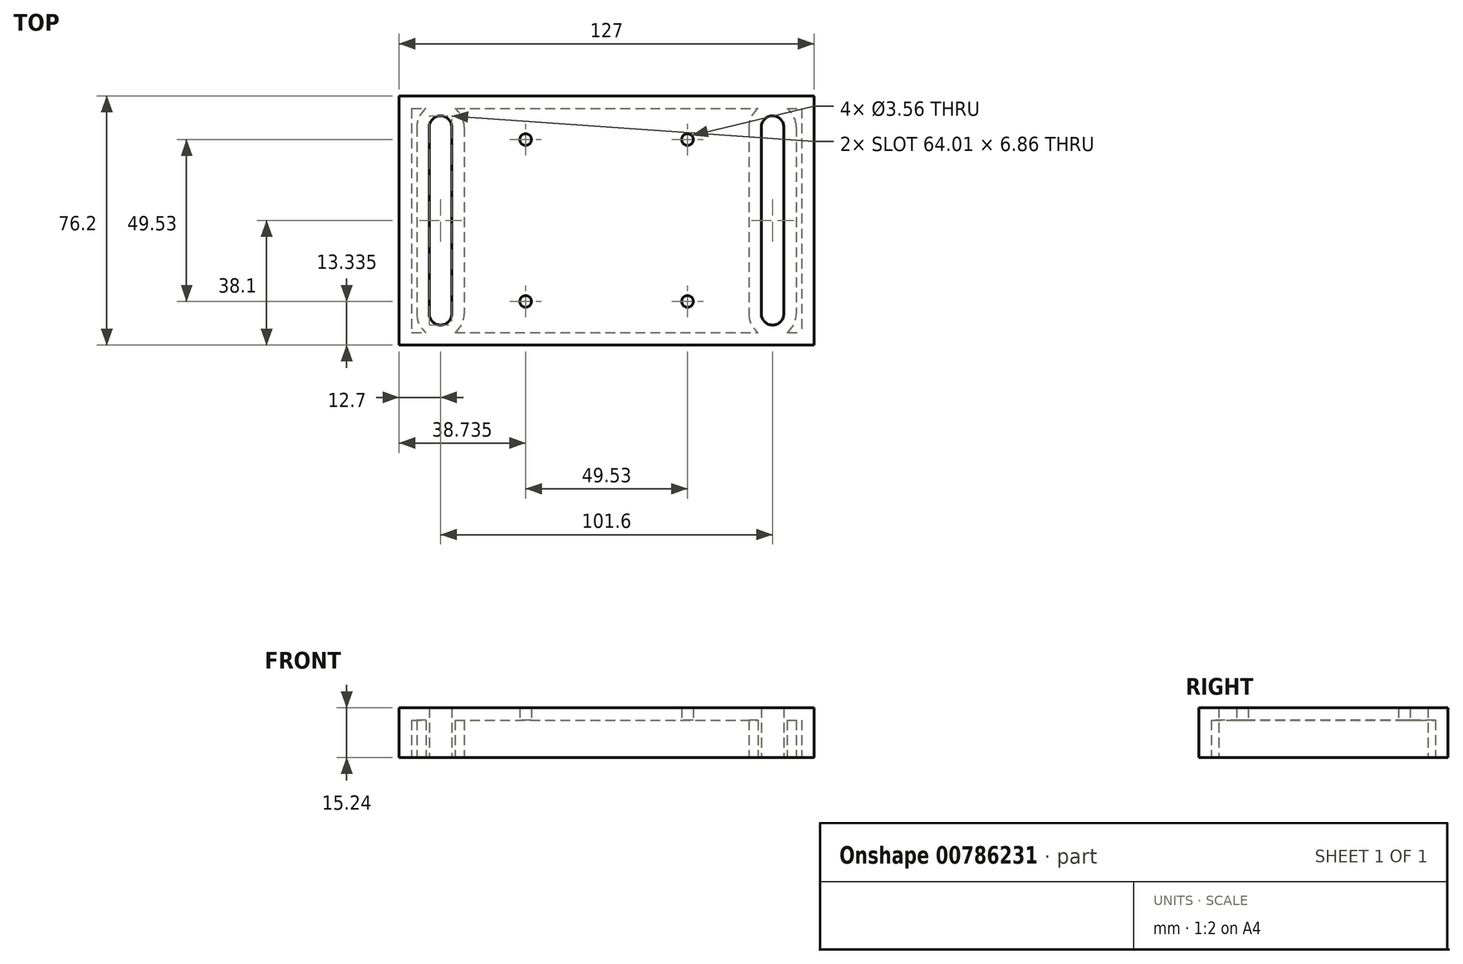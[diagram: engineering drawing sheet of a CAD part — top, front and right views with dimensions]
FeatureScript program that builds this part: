
annotation { "Feature Type Name" : "Feature", "Feature Type Description" : "" }
export const myFeature = defineFeature(function(context is Context, id is Id, definition is map)
    precondition{}
    {
        {
            var Q0;
            Q0=qCreatedBy(makeId("Top.planeOp"),FACE);
            var sketch = newSketch(context, id + "F0", { "sketchPlane" : qUnion([Q0])});
            skLineSegment(sketch, "E0.bottom", {"start": v(-63.5, 38.1) * mm, "end": v(63.5, 38.1) * mm});
            skLineSegment(sketch, "E0.top", {"start": v(-63.5, -38.1) * mm, "end": v(63.5, -38.1) * mm});
            skLineSegment(sketch, "E0.left", {"start": v(-63.5, 38.1) * mm, "end": v(-63.5, -38.1) * mm});
            skLineSegment(sketch, "E0.right", {"start": v(63.5, 38.1) * mm, "end": v(63.5, -38.1) * mm});
            skSolve(sketch);
        }
        {
            var Q0;
            Q0 = qSketchRegion(id + "F0", true);
            extrude(context, id + "F1", {"entities" : qUnion([Q0]), "depth" : 15.24 * mm, "offsetDistance" : 25.4 * mm});
        }
        {
            var Q0;
            Q0=qCreatedBy(makeId("Top.planeOp"),FACE);
            var sketch = newSketch(context, id + "F2", { "sketchPlane" : qUnion([Q0])});
            skLineSegment(sketch, "E1.left", {"start": v(-54.23, 28.58) * mm, "end": v(-54.23, -28.58) * mm});
            skLineSegment(sketch, "E1.right", {"start": v(-47.37, 28.58) * mm, "end": v(-47.37, -28.58) * mm});
            skLineSegment(sketch, "E2.left", {"start": v(47.37, 28.58) * mm, "end": v(47.37, -28.58) * mm});
            skLineSegment(sketch, "E2.right", {"start": v(54.23, 28.58) * mm, "end": v(54.23, -28.58) * mm});
            skArc(sketch, "E3", {"start": v(-47.37, 28.58) * mm, "mid": v(-50.8, 32) * mm, "end": v(-54.23, 28.58) * mm});
            skArc(sketch, "E4", {"start": v(-54.23, -28.58) * mm, "mid": v(-50.8, -32) * mm, "end": v(-47.37, -28.58) * mm});
            skArc(sketch, "E5", {"start": v(47.37, -28.58) * mm, "mid": v(50.8, -32) * mm, "end": v(54.23, -28.58) * mm});
            skArc(sketch, "E6", {"start": v(54.23, 28.58) * mm, "mid": v(50.8, 32) * mm, "end": v(47.37, 28.58) * mm});
            skSolve(sketch);
        }
        {
            var Q0;
            Q0 = qSketchRegion(id + "F2", true);
            extrude(context, id + "F3", {"entities" : qUnion([Q0]), "operationType" : NewBodyOperationType.REMOVE, "endBound" : BoundingType.THROUGH_ALL, "depth" : 25.4 * mm, "offsetDistance" : 25.4 * mm});
        }
        {
            var Q0;
            Q0=makeQuery(id+"F1.opExtrude","CAP_FACE",FACE,{"disambiguationData":[OSD([sQuery(id+"F0.wireOp",EDGE,"E0.bottom"),sQuery(id+"F0.wireOp",EDGE,"E0.top"),sQuery(id+"F0.wireOp",EDGE,"E0.left"),sQuery(id+"F0.wireOp",EDGE,"E0.right")])],"isStart":true});
            shell(context, id + "F4", {"entities" : qUnion([Q0]), "thickness" : 3.8 * mm});
        }
        {
            var Q0;
            Q0=qCreatedBy(makeId("Top.planeOp"),FACE);
            var sketch = newSketch(context, id + "F5", { "sketchPlane" : qUnion([Q0])});
            skCircle(sketch, "E7", {"center": v(-24.77, 24.77) * mm, "radius": 1.78 * mm});
            skCircle(sketch, "E8", {"center": v(24.77, 24.77) * mm, "radius": 1.78 * mm});
            skCircle(sketch, "E9", {"center": v(-24.77, -24.77) * mm, "radius": 1.78 * mm});
            skCircle(sketch, "E10", {"center": v(24.77, -24.77) * mm, "radius": 1.78 * mm});
            skSolve(sketch);
        }
        {
            var Q0;
            Q0 = qSketchRegion(id + "F5", true);
            extrude(context, id + "F6", {"entities" : qUnion([Q0]), "operationType" : NewBodyOperationType.REMOVE, "endBound" : BoundingType.THROUGH_ALL, "depth" : 15.24 * mm, "offsetDistance" : 25.4 * mm});
        }
    });
